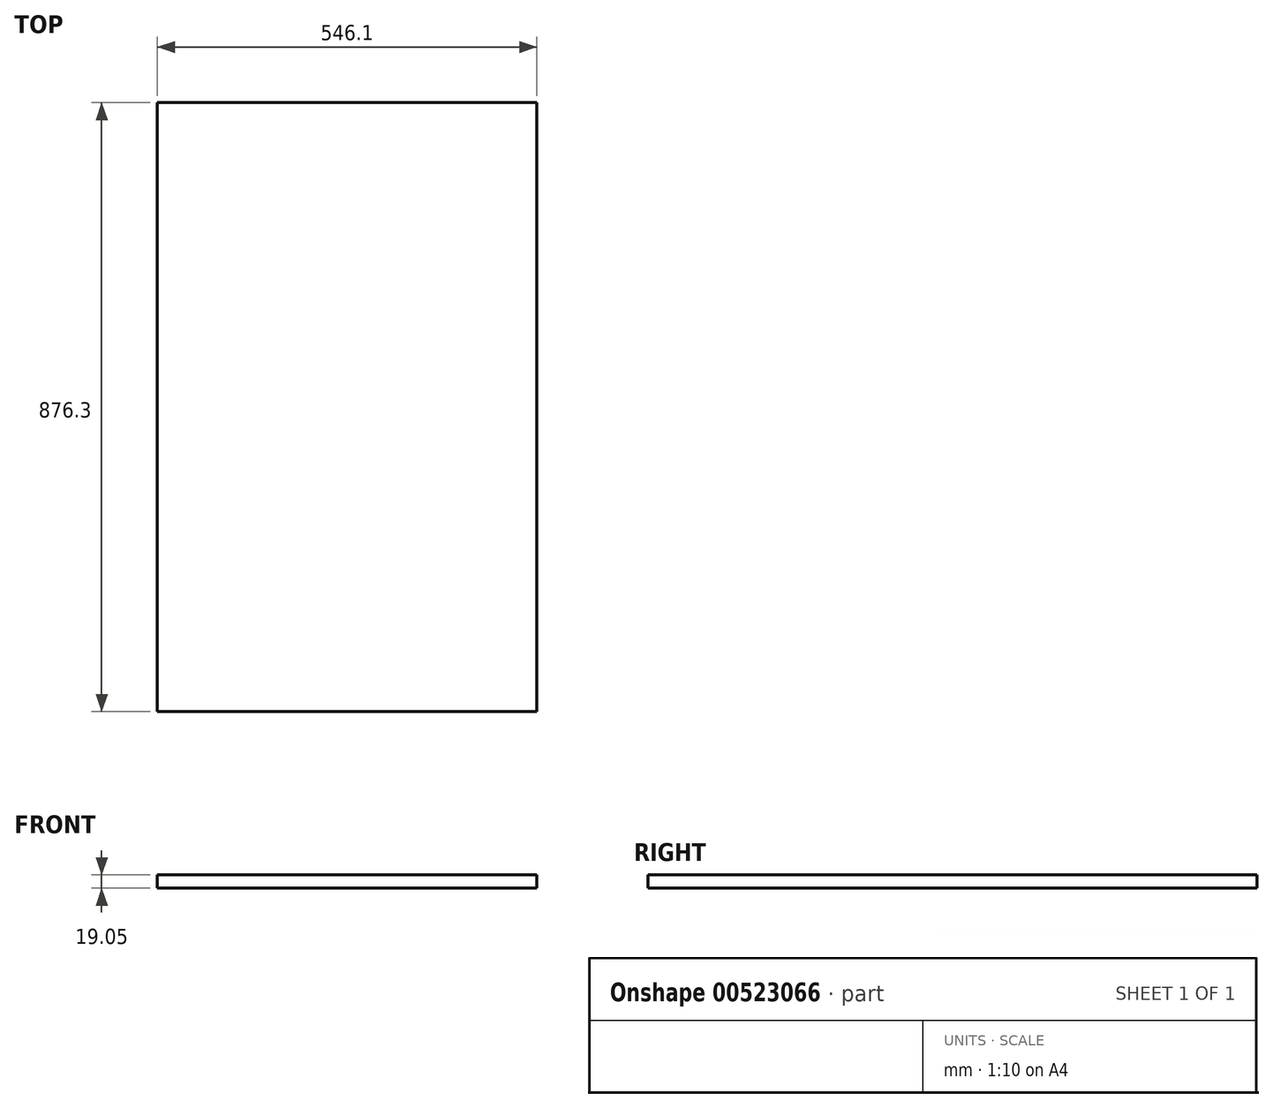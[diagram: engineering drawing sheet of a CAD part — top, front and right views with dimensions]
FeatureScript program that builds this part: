
annotation { "Feature Type Name" : "Feature", "Feature Type Description" : "" }
export const myFeature = defineFeature(function(context is Context, id is Id, definition is map)
    precondition{}
    {
        {
            var Q0;
            Q0=qCreatedBy(makeId("Top.planeOp"),FACE);
            var sketch = newSketch(context, id + "F0", { "sketchPlane" : qUnion([Q0])});
            skLineSegment(sketch, "E0.bottom", {"start": v(0, 0) * mm, "end": v(546.1, 0) * mm});
            skLineSegment(sketch, "E0.top", {"start": v(0, 876.3) * mm, "end": v(546.1, 876.3) * mm});
            skLineSegment(sketch, "E0.left", {"start": v(0, 0) * mm, "end": v(0, 876.3) * mm});
            skLineSegment(sketch, "E0.right", {"start": v(546.1, 0) * mm, "end": v(546.1, 876.3) * mm});
            skSolve(sketch);
        }
        {
            var Q0;
            Q0=qSketchRegion(id+"F0",true);
            extrude(context, id + "F1", {"entities" : qUnion([Q0]), "depth" : 19.05 * mm, "offsetDistance" : 25.4 * mm});
        }
    });
